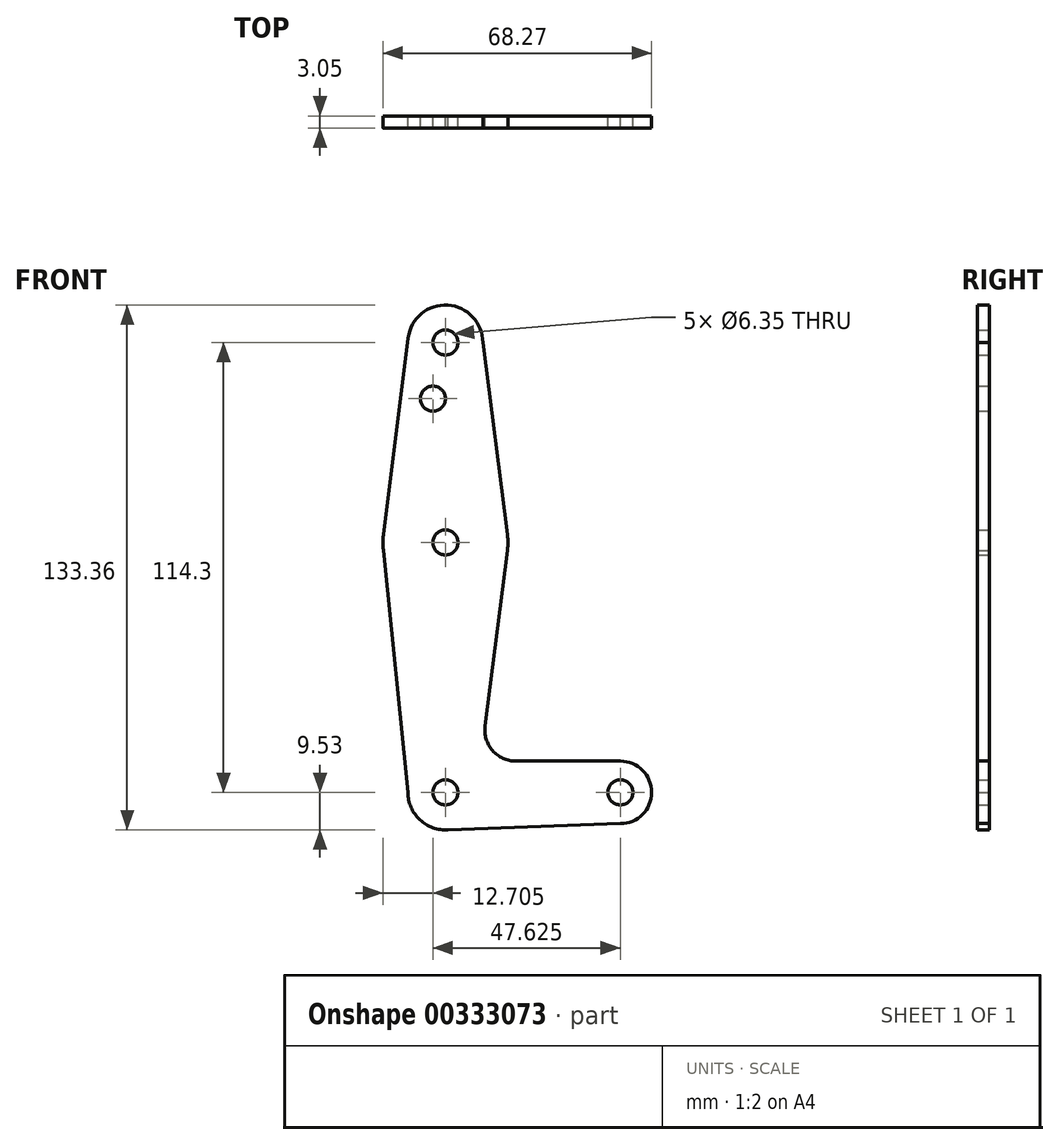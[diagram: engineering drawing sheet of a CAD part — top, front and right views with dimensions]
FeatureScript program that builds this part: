
annotation { "Feature Type Name" : "Feature", "Feature Type Description" : "" }
export const myFeature = defineFeature(function(context is Context, id is Id, definition is map)
    precondition{}
    {
        {
            var Q0;
            Q0=qCreatedBy(makeId("Front.planeOp"),FACE);
            var sketch = newSketch(context, id + "F0", { "sketchPlane" : qUnion([Q0])});
            skLineSegment(sketch, "E0", {"start": v(0, 0) * mm, "end": v(0, 114.3) * mm, "construction": true});
            skCircle(sketch, "E1", {"center": v(0, 63.5) * mm, "radius": 15.88 * mm});
            skCircle(sketch, "E2", {"center": v(0, 0) * mm, "radius": 9.53 * mm});
            skLineSegment(sketch, "E3", {"start": v(0, 0) * mm, "end": v(44.45, 0) * mm, "construction": true});
            skCircle(sketch, "E4", {"center": v(0, 114.3) * mm, "radius": 9.53 * mm});
            skCircle(sketch, "E5", {"center": v(44.45, 0) * mm, "radius": 7.94 * mm});
            skLineSegment(sketch, "E6", {"start": v(9.53, 114.3) * mm, "end": v(15.75, 65.5) * mm});
            skLineSegment(sketch, "E7", {"start": v(-15.75, 65.5) * mm, "end": v(-9.45, 115.5) * mm});
            skCircle(sketch, "E8", {"center": v(0, 63.5) * mm, "radius": 3.18 * mm});
            skCircle(sketch, "E9", {"center": v(44.45, 0) * mm, "radius": 3.18 * mm});
            skCircle(sketch, "E10", {"center": v(0, 114.3) * mm, "radius": 3.18 * mm});
            skCircle(sketch, "E11", {"center": v(0, 0) * mm, "radius": 3.18 * mm});
            skCircle(sketch, "E12", {"center": v(-3.18, 100.03) * mm, "radius": 3.18 * mm});
            skLineSegment(sketch, "E13", {"start": v(-15.75, 61.5) * mm, "end": v(-9.52, 0) * mm});
            skLineSegment(sketch, "E14", {"start": v(15.75, 61.5) * mm, "end": v(10.06, 16.9) * mm});
            skLineSegment(sketch, "E15", {"start": v(17.95, 7.94) * mm, "end": v(44.45, 7.94) * mm});
            skLineSegment(sketch, "E16", {"start": v(0, -9.52) * mm, "end": v(44.45, -7.94) * mm});
            skArc(sketch, "E17.filletArc", {"start": v(10.06, 16.9) * mm, "mid": v(11.98, 10.63) * mm, "end": v(17.95, 7.94) * mm});
            skSolve(sketch);
        }
        {
            var Q0;
            Q0 = qSketchRegion(id + "F0", true);
            extrude(context, id + "F1", {"entities" : qUnion([Q0]), "depth" : 3.05 * mm});
        }
    });
